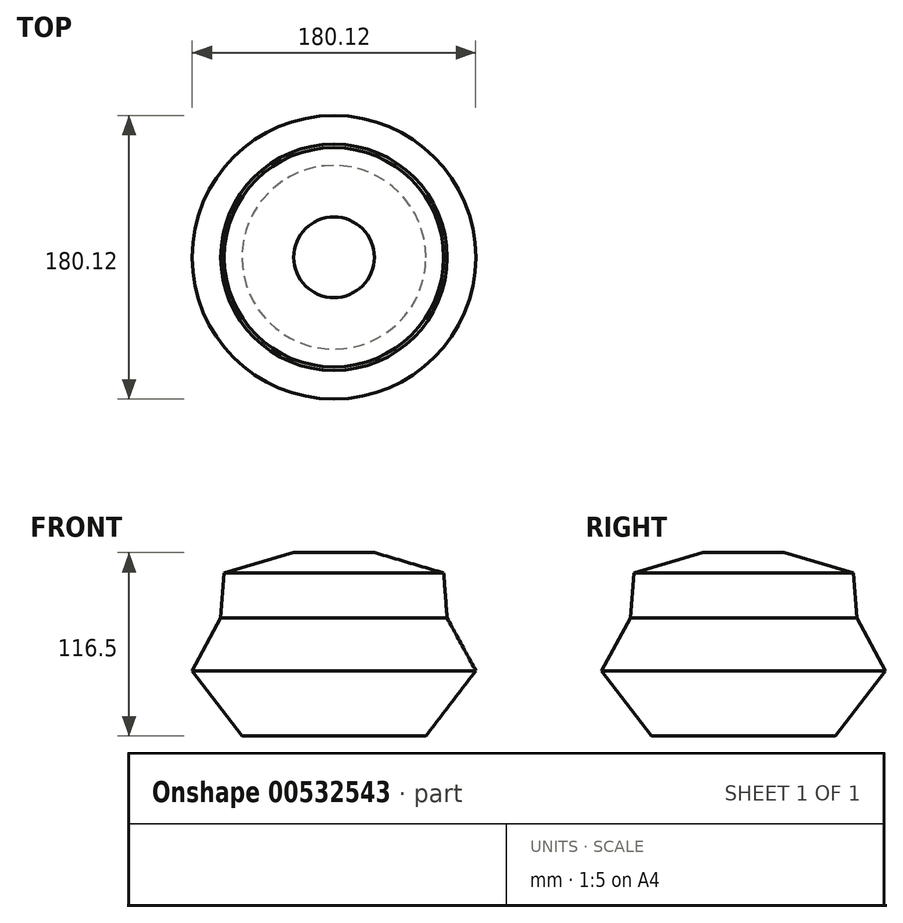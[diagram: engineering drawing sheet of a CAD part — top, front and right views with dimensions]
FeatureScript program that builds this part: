
annotation { "Feature Type Name" : "Feature", "Feature Type Description" : "" }
export const myFeature = defineFeature(function(context is Context, id is Id, definition is map)
    precondition{}
    {
        {
            var Q0;
            Q0=qCreatedBy(makeId("Front.planeOp"),FACE);
            var sketch = newSketch(context, id + "F0", { "sketchPlane" : qUnion([Q0])});
            skLineSegment(sketch, "E0", {"start": v(0, 0) * mm, "end": v(-58.39, 0) * mm});
            skLineSegment(sketch, "E1", {"start": v(-58.39, 0) * mm, "end": v(-90.06, 41.31) * mm});
            skLineSegment(sketch, "E2", {"start": v(-90.06, 41.31) * mm, "end": v(-71.88, 74.91) * mm});
            skLineSegment(sketch, "E3", {"start": v(-71.88, 74.91) * mm, "end": v(-69.68, 103.56) * mm});
            skLineSegment(sketch, "E4", {"start": v(-69.68, 103.56) * mm, "end": v(-25.61, 116.5) * mm});
            skLineSegment(sketch, "E5", {"start": v(-25.61, 116.5) * mm, "end": v(0, 116.5) * mm});
            skLineSegment(sketch, "E6", {"start": v(0, 116.5) * mm, "end": v(0, 0) * mm});
            skSolve(sketch);
        }
        {
            var Q0;
            Q0=makeQuery(id+"F0.imprint","IMPRINT",FACE,{"disambiguationData":[TD([[makeQuery(id+"F0.imprint","IMPRINT",EDGE,{"derivedFrom":sQuery(id+"F0.wireOp",EDGE,"E0")}),-1.0]])]});
            var Q1;
            Q1=sQuery(id+"F0.wireOp",EDGE,"E6");
            revolve(context, id + "F1", {"entities" : qUnion([Q0]), "axis" : qUnion([Q1]), "revolveType" : RevolveType.FULL});
        }
    });
